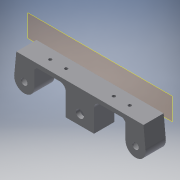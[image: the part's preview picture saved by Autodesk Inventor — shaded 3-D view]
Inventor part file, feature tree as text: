
AUTODESK INVENTOR PART (.ipt)
format: ipt  version: 2016 (Build 200138000, 138)  size: 201,728 bytes
history: native  units: in
note: dims shown in document units (in); Inventor stores cm internally (conversion verified against a paired STEP export)
features: reference x7, extrude x4, sketch x4, fillet x2, plane x1, chamfer x1
ambient origin geometry x8: Origin, YZ Plane, XZ Plane, XY Plane, X Axis, Y Axis, Z Axis, Center Point
bodies: Solid1 (feature_tree)
feature tree (19):
  plane  "Work Plane1"
  extrude  "Extrusion1"  Depth=1.4in
  extrude  "Extrusion2"  Depth=1.0in TaperAngle=0.0deg
  extrude  "Extrusion3"  Depth=0.9449in
  fillet  "Fillet1"  Radius=0.9449in
  extrude  "Extrusion4"  Depth=0.4in
  chamfer  "Chamfer1"  Distance=0.4in
  fillet  "Fillet2"  Radius=0.425in
  sketch  "Sketch1"  dims[d0=0.4in d2=1.4in]
  reference  "Reference1"
  reference  "Reference2"
  reference  "Reference3"
  reference  "Reference4"
  sketch  "Sketch2"  dims[d3=1.0in d5=1.0in d6=0.0in]
  reference  "Reference5"
  reference  "Reference6"
  sketch  "Sketch3"  dims[d7=0.5906in d8=0.5906in d9=0.9449in d10=0.0in]
  sketch  "Sketch4"  dims[d11=0.2in d12=0.4in d13=0.4in d14=0.425in d15=0.85in d16=0.85in d17=0.14in d18=0.4in d19=0.1in d20=0.85in d21=0.0in d22=0.425in d23=1.1811in d24=0.7874in d25=0.1575in d26=0.1575in d27=1.0in d28=0.0in d29=0.125in d30=0.125in d31=45.0deg d32=0.3in]
  reference  "Reference7"
